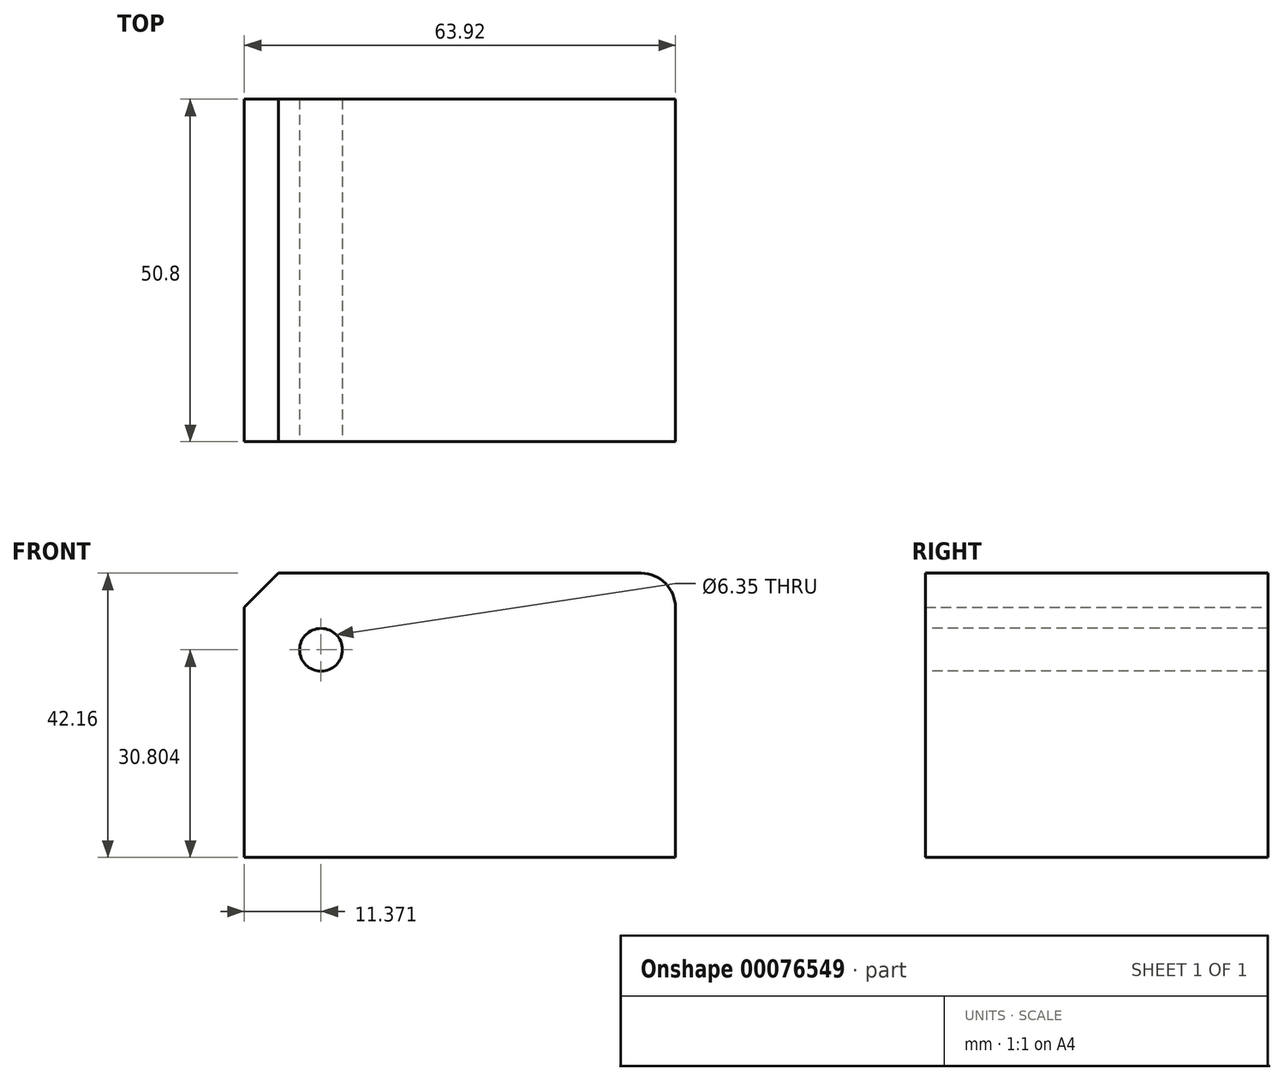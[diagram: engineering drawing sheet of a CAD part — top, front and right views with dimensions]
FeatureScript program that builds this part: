
annotation { "Feature Type Name" : "Feature", "Feature Type Description" : "" }
export const myFeature = defineFeature(function(context is Context, id is Id, definition is map)
    precondition{}
    {
        {
            var Q0;
            Q0=qCreatedBy(makeId("Front.planeOp"),FACE);
            var sketch = newSketch(context, id + "F0", { "sketchPlane" : qUnion([Q0])});
            skLineSegment(sketch, "E0", {"start": v(-27.31, 23.8) * mm, "end": v(-27.31, -18.36) * mm});
            skLineSegment(sketch, "E1", {"start": v(-27.31, -18.36) * mm, "end": v(36.6, -18.36) * mm});
            skLineSegment(sketch, "E2", {"start": v(36.6, -18.36) * mm, "end": v(36.6, 23.8) * mm});
            skLineSegment(sketch, "E3", {"start": v(-27.31, 23.8) * mm, "end": v(36.6, 23.8) * mm});
            skSolve(sketch);
        }
        {
            var Q0;
            Q0=makeQuery(id+"F0.imprint","IMPRINT",FACE,{"disambiguationData":[TD([[makeQuery(id+"F0.imprint","IMPRINT",EDGE,{"derivedFrom":sQuery(id+"F0.wireOp",EDGE,"E0")}),1.0]])]});
            extrude(context, id + "F1", {"entities" : qUnion([Q0]), "depth" : 50.8 * mm});
        }
        {
            var Q0;
            Q0=makeQuery(id+"F1.opExtrude","CAP_FACE",FACE,{"disambiguationData":[OSD([sQuery(id+"F0.wireOp",EDGE,"E0"),sQuery(id+"F0.wireOp",EDGE,"E1"),sQuery(id+"F0.wireOp",EDGE,"E2"),sQuery(id+"F0.wireOp",EDGE,"E3")])],"isStart":false});
            var sketch = newSketch(context, id + "F2", { "sketchPlane" : qUnion([Q0])});
            skCircle(sketch, "E4", {"center": v(-15.94, 12.44) * mm, "radius": 6.8 * mm});
            skSolve(sketch);
        }
        {
            var Q0;
            Q0=sQuery(id+"F2.wireOp",VERTEX,"E4.center");
            var Q1;
            Q1=makeQuery(id+"F1.opExtrude","SWEPT_BODY",BODY,{"disambiguationData":[OSD([sQuery(id+"F0.wireOp",EDGE,"E0"),sQuery(id+"F0.wireOp",EDGE,"E1"),sQuery(id+"F0.wireOp",EDGE,"E2"),sQuery(id+"F0.wireOp",EDGE,"E3")])]});
            hole(context, id + "F3", {"style" : HoleStyle.SIMPLE, "endStyle" : HoleEndStyle.THROUGH, "holeDiameter" : 6.35 * mm, "locations" : qUnion([Q0]), "scope" : qUnion([Q1]), "isTappedThrough" : true});
        }
        {
            var Q0;
            Q0=makeQuery(id+"F1.opExtrude","SWEPT_EDGE",EDGE,{"disambiguationData":[OSD([sQuery(id+"F0.wireOp",EDGE,"E2"),sQuery(id+"F0.wireOp",EDGE,"E3")])]});
            fillet(context, id + "F4", {"entities" : qUnion([Q0]), "radius" : 5.08 * mm, "tangentPropagation" : true, "allowEdgeOverflow" : false});
        }
        {
            var Q0;
            Q0=makeQuery(id+"F1.opExtrude","SWEPT_EDGE",EDGE,{"disambiguationData":[OSD([sQuery(id+"F0.wireOp",EDGE,"E0"),sQuery(id+"F0.wireOp",EDGE,"E3")])]});
            chamfer(context, id + "F5", {"entities" : qUnion([Q0]), "width" : 5.08 * mm, "tangentPropagation" : true});
        }
    });
